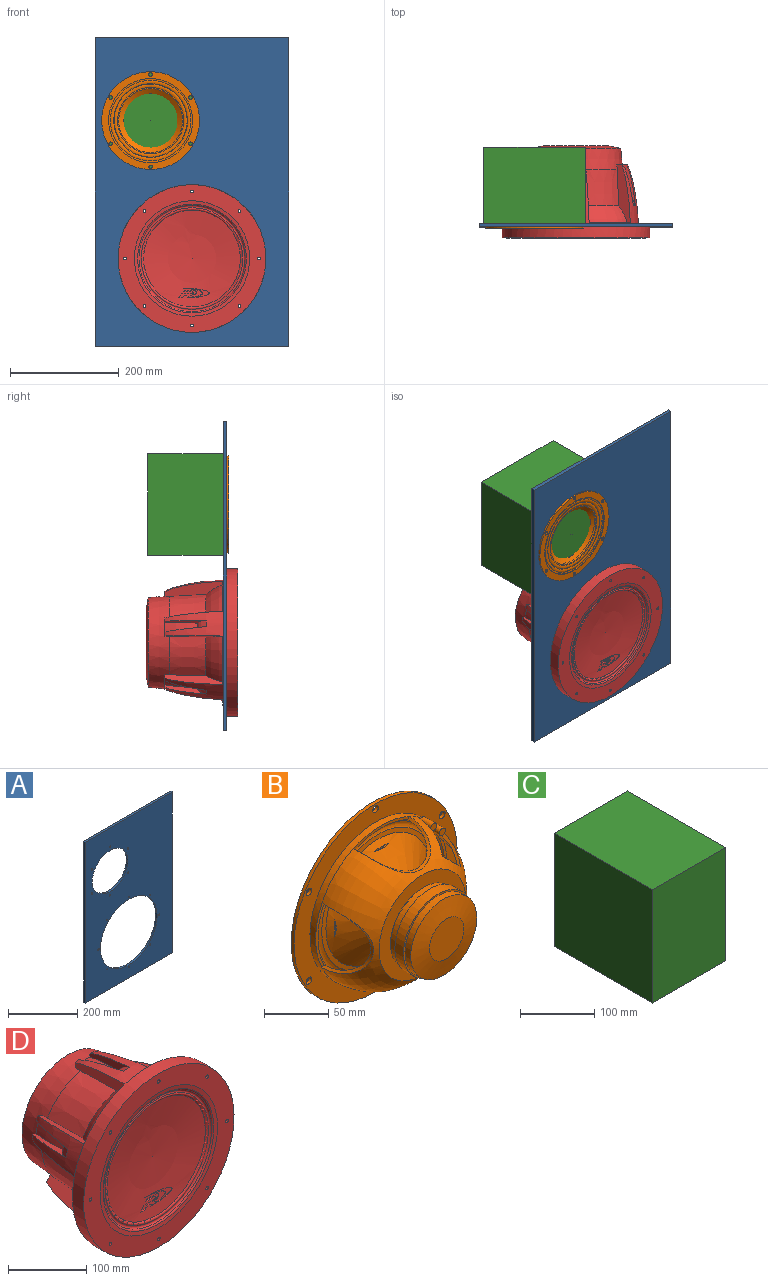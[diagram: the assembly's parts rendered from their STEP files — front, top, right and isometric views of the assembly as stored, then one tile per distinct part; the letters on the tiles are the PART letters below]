
ASSEMBLY  parts=4 mates=2
PART A: 22 faces, bbox 355.6x6.4x567.8 mm
  f0: plane 567.8x6.35mm, normal (-1,0,0), area 3605.5mm2, adj f1,f3,f4,f5
  f1: plane 355.6x6.35mm, normal (0,0,1), area 2258.1mm2, adj f0,f2,f4,f5
  f2: plane 567.8x6.35mm, normal (1,0,0), area 3605.5mm2, adj f1,f3,f4,f5
  f3: plane 355.6x6.35mm, normal (0,0,-1), area 2258.1mm2, adj f0,f2,f4,f5
  f4: plane 567.8x355.6mm, normal (0,1,0), area 143146.8mm2, adj f0,f1,f2,f3,f6,f7,f8,f9
  f5: plane 567.8x355.6mm, normal (0,-1,0), area 143146.8mm2, adj f0,f1,f2,f3,f6,f7,f8,f9
  f6: cylinder r=72.52mm len=145.03mm, axis (0,-1,0), area 2893.3mm2, adj f4,f5
  f7: cylinder r=2.38mm len=6.35mm, axis (0,-1,0), area 95mm2, adj f4,f5
  f8: cylinder r=2.38mm len=6.35mm, axis (0,-1,0), area 95mm2, adj f4,f5
  f9: cylinder r=2.38mm len=6.35mm, axis (0,-1,0), area 95mm2, adj f4,f5
  f10: cylinder r=2.38mm len=6.35mm, axis (0,-1,0), area 95mm2, adj f4,f5
  f11: cylinder r=2.38mm len=6.35mm, axis (0,-1,0), area 95mm2, adj f4,f5
  f12: cylinder r=2.38mm len=6.35mm, axis (0,-1,0), area 95mm2, adj f4,f5
  f13: cylinder r=2.38mm len=6.35mm, axis (0,-1,0), area 95mm2, adj f4,f5
  f14: cylinder r=3.17mm len=6.35mm, axis (0,-1,0), area 126.7mm2, adj f4,f5
  f15: cylinder r=3.17mm len=6.35mm, axis (0,-1,0), area 126.7mm2, adj f4,f5
  f16: cylinder r=3.17mm len=6.35mm, axis (0,-1,0), area 126.7mm2, adj f4,f5
  f17: cylinder r=115.5mm len=231mm, axis (0,-1,0), area 4608.2mm2, adj f4,f5
  f18: cylinder r=3.17mm len=6.35mm, axis (0,-1,0), area 126.7mm2, adj f4,f5
  f19: cylinder r=3.17mm len=6.35mm, axis (0,-1,0), area 126.7mm2, adj f4,f5
  f20: cylinder r=3.17mm len=6.35mm, axis (0,-1,0), area 126.7mm2, adj f4,f5
  f21: cylinder r=2.38mm len=6.35mm, axis (0,-1,0), area 95mm2, adj f4,f5
PART B: 78 faces, bbox 180.1x81.7x180.1 mm
  f0: plane 6.14x4.89mm, normal (0,-1,0), area 13mm2, adj f10,f38,f51,f69
  f1: plane 7.38x7.38mm, normal (0,-1,0), area 19.2mm2, adj f10,f38,f65,f69
  f2: plane 6.14x4.89mm, normal (0,-1,0), area 13mm2, adj f10,f38,f50,f65
  f3: plane 13.36x13.36mm, normal (0,-1,0), area 140.2mm2, adj f4
  f4: torus R=6.68mm, axis (0,-1,0), area 421.3mm2, adj f3,f5
  f5: cone r=13.01mm half-angle=54.8deg, axis (0,1,0), area 11955.4mm2, adj f4,f6,f19,f20,f54,f55,f58,f59
  f6: cone r=61.59mm half-angle=84.5deg, axis (0,1,0), area 1563.3mm2, adj f5,f7
  f7: torus R=64.94mm, axis (0,-1,0), area 2086.2mm2, adj f6,f8
  f8: torus R=67.45mm, axis (0,-1,0), area 994.8mm2, adj f7,f9
  f9: torus R=71.9mm, axis (0,-1,0), area 496.2mm2, adj f8,f10
  f10: cylinder r=69.98mm len=139.95mm, axis (0,-1,0), area 2383.7mm2, adj f0,f1,f2,f9,f11,f17,f52,f56
  f11: torus R=18.17mm, axis (0,-1,0), area 10126.2mm2, adj f10,f12,f18,f49,f50,f51,f53,f57
  f12: torus R=42.46mm, axis (0,-1,0), area 2789.7mm2, adj f11,f13
  f13: torus R=33.02mm, axis (0,-1,0), area 2169.8mm2, adj f12,f14
  f14: torus R=23.59mm, axis (0,-1,0), area 1549.9mm2, adj f13,f15
  f15: torus R=14.15mm, axis (0,-1,0), area 929.9mm2, adj f14,f16
  f16: torus R=4.72mm, axis (0,-1,0), area 310mm2, adj f15
  f17: plane 61.73x8.91mm, normal (0,-1,0), area 157.5mm2, adj f10,f18,f38
  f18: cone r=38.1mm half-angle=1deg, axis (0,1,0), area 339.7mm2, adj f11,f17,f37
  f19: cone r=38.1mm half-angle=1deg, axis (0,1,0), area 9.7mm2, adj f5,f20
  f20: plane 15.49x1.35mm, normal (0,-1,0), area 14mm2, adj f5,f19
  f21: torus R=9.58mm, axis (0,-1,0), area 22.9mm2, adj f22,f48
  f22: cone r=23.77mm half-angle=30deg, axis (0,1,0), area 2987.6mm2, adj f21,f23
  f23: plane 47.54x47.54mm, normal (0,1,0), area 43.5mm2, adj f22,f24
  f24: cone r=8.84mm half-angle=30deg, axis (0,1,0), area 2971.2mm2, adj f23,f25
  f25: torus R=8.67mm, axis (0,-1,0), area 25.6mm2, adj f24,f26
  f26: cone r=0mm half-angle=15deg, axis (0,-1,0), area 872.6mm2, adj f25
  f27: plane 38.1x38.1mm, normal (0,-1,0), area 1140.1mm2, adj f28
  f28: cone r=19.05mm half-angle=79.7deg, axis (0,1,0), area 3098.1mm2, adj f27,f29
  f29: cylinder r=36.51mm len=73.03mm, axis (0,-1,0), area 1456.8mm2, adj f28,f30
  f30: plane 76.2x76.2mm, normal (0,-1,0), area 372.1mm2, adj f29,f31
  f31: cylinder r=38.1mm len=76.2mm, axis (0,-1,0), area 2280.2mm2, adj f30,f32
  f32: plane 76.2x76.2mm, normal (0,1,0), area 372.1mm2, adj f31,f33
  f33: cylinder r=36.51mm len=73.03mm, axis (0,-1,0), area 1456.8mm2, adj f32,f34
  f34: plane 73.03x73.03mm, normal (0,1,0), area 286.3mm2, adj f33,f35
  f35: cylinder r=35.24mm len=70.49mm, axis (0,-1,0), area 281.2mm2, adj f34,f36
  f36: plane 95.89x95.89mm, normal (0,-1,0), area 3318.9mm2, adj f35,f37
  f37: torus R=18.17mm, axis (0,-1,0), area 10575mm2, adj f18,f36,f38,f49,f50,f51,f53,f57
  f38: cylinder r=72.52mm len=145.03mm, axis (0,-1,0), area 2893.3mm2, adj f0,f1,f2,f17,f37,f39,f52,f56
  f39: plane 180.09x180.09mm, normal (0,-1,0), area 8760.5mm2, adj f38,f40,f72,f73,f74,f75,f76,f77
  f40: cylinder r=90.04mm len=180.09mm, axis (0,-1,0), area 1796.3mm2, adj f39,f41
  f41: plane 180.09x180.09mm, normal (0,1,0), area 6488.4mm2, adj f40,f42,f72,f73,f74,f75,f76,f77
  f42: cylinder r=77.34mm len=154.69mm, axis (0,-1,0), area 617.2mm2, adj f41,f43
  f43: cone r=77.34mm half-angle=84.5deg, axis (0,1,0), area 1511.8mm2, adj f42,f44
  f44: torus R=71.9mm, axis (0,-1,0), area 2884.4mm2, adj f43,f45
  f45: torus R=67.45mm, axis (0,-1,0), area 279.6mm2, adj f44,f46
  f46: torus R=64.94mm, axis (0,-1,0), area 2601.4mm2, adj f45,f47
  f47: cone r=60.9mm half-angle=84.5deg, axis (0,1,0), area 778.2mm2, adj f46,f48
  f48: cone r=9.66mm half-angle=54.8deg, axis (0,1,0), area 12942.8mm2, adj f21,f47
  f49: plane 20.3x20.3mm, normal (0.71,0.02,0.71), area 99mm2, adj f11,f37,f50,f51
  f50: plane 38.95x12.32mm, normal (-0.71,0.02,0.71), area 107.3mm2, adj f2,f11,f37,f49
  f51: plane 38.95x12.32mm, normal (0.71,0.02,-0.71), area 107.3mm2, adj f0,f11,f37,f49
  f52: plane 61.73x8.91mm, normal (0,-1,0), area 157.5mm2, adj f10,f38,f53
  f53: cone r=38.1mm half-angle=1deg, axis (0,1,0), area 339.3mm2, adj f11,f37,f52
  f54: plane 15.49x1.35mm, normal (0,-1,0), area 14mm2, adj f5,f55
  f55: cone r=38.1mm half-angle=1deg, axis (0,1,0), area 9.7mm2, adj f5,f54
  f56: plane 61.73x8.91mm, normal (0,-1,0), area 157.5mm2, adj f10,f38,f57
  f57: cone r=38.1mm half-angle=1deg, axis (0,1,0), area 339.3mm2, adj f11,f37,f56
  f58: plane 15.49x1.35mm, normal (0,-1,0), area 14mm2, adj f5,f59
  f59: cone r=38.1mm half-angle=1deg, axis (0,1,0), area 9.7mm2, adj f5,f58
  f60: plane 61.73x8.91mm, normal (0,-1,0), area 157.5mm2, adj f10,f38,f61
  f61: cone r=38.1mm half-angle=1deg, axis (0,1,0), area 339.3mm2, adj f11,f37,f60
  f62: plane 15.49x1.35mm, normal (0,-1,0), area 14mm2, adj f5,f63
  f63: cone r=38.1mm half-angle=1deg, axis (0,1,0), area 9.7mm2, adj f5,f62
  f64: plane 4.41x3.83mm, normal (0,1,0), area 6.6mm2, adj f38,f65
  f65: cone r=3.17mm half-angle=1deg, axis (0,-1,0), area 262.2mm2, adj f1,f2,f64,f66,f67
  f66: plane 6.79x6.79mm, normal (0,-1,0), area 36.2mm2, adj f65
  f67: plane 4.8x4.24mm, normal (0,1,0), area 9.4mm2, adj f10,f65
  f68: plane 4.41x3.83mm, normal (0,1,0), area 6.6mm2, adj f38,f69
  f69: cone r=3.17mm half-angle=1deg, axis (0,-1,0), area 262.2mm2, adj f0,f1,f68,f70,f71
  f70: plane 6.79x6.79mm, normal (0,-1,0), area 36.2mm2, adj f69
  f71: plane 4.8x4.24mm, normal (0,1,0), area 9.4mm2, adj f10,f69
  f72: cylinder r=3.17mm len=6.35mm, axis (0,1,0), area 63.3mm2, adj f39,f41
  f73: cylinder r=3.17mm len=6.35mm, axis (0,1,0), area 63.3mm2, adj f39,f41
  f74: cylinder r=3.17mm len=6.35mm, axis (0,1,0), area 63.3mm2, adj f39,f41
  f75: cylinder r=3.17mm len=6.35mm, axis (0,1,0), area 63.3mm2, adj f39,f41
  f76: cylinder r=3.17mm len=6.35mm, axis (0,1,0), area 63.3mm2, adj f39,f41
  f77: cylinder r=3.17mm len=6.35mm, axis (0,1,0), area 63.3mm2, adj f39,f41
PART C: 6 faces, bbox 139.7x187.3x187.3 mm
  f0: plane 187.33x187.33mm, normal (1,0,0), area 35090.7mm2, adj f1,f2,f3,f4
  f1: plane 187.33x139.7mm, normal (0,0,-1), area 26169.3mm2, adj f0,f2,f3,f5
  f2: plane 187.33x139.7mm, normal (0,-1,0), area 26169.3mm2, adj f0,f1,f4,f5
  f3: plane 187.33x139.7mm, normal (0,1,0), area 26169.3mm2, adj f0,f1,f4,f5
  f4: plane 187.33x139.7mm, normal (0,0,1), area 26169.3mm2, adj f0,f2,f3,f5
  f5: plane 187.33x187.33mm, normal (-1,0,0), area 35090.7mm2, adj f1,f2,f3,f4
PART D: 90 faces, bbox 274.1x171.5x274.1 mm
  f0: cylinder r=2.38mm len=20.4mm, axis (0,-1,0), area 305.2mm2, adj f8,f68
  f1: cylinder r=2.38mm len=20.4mm, axis (0,-1,0), area 305.2mm2, adj f8,f68
  f2: cylinder r=2.38mm len=20.4mm, axis (0,-1,0), area 305.2mm2, adj f8,f68
  f3: cylinder r=2.38mm len=20.4mm, axis (0,-1,0), area 305.2mm2, adj f8,f68
  f4: cylinder r=2.38mm len=20.4mm, axis (0,-1,0), area 305.2mm2, adj f8,f68
  f5: cylinder r=2.38mm len=20.4mm, axis (0,-1,0), area 305.2mm2, adj f8,f68
  f6: cylinder r=2.38mm len=20.4mm, axis (0,-1,0), area 305.2mm2, adj f8,f68
  f7: cylinder r=136mm len=272mm, axis (0,-1,0), area 17432.1mm2, adj f8,f68
  f8: plane 272x272mm, normal (0,1,0), area 16054.8mm2, adj f0,f1,f2,f3,f4,f5,f6,f7
  f9: plane 108.77x32.45mm, normal (0.1,0.03,-1), area 1820.9mm2, adj f11,f12,f54,f65,f66,f67
  f10: plane 108.77x26.73mm, normal (-0.51,0.03,0.86), area 1820.9mm2, adj f11,f12,f18,f57,f58,f67
  f11: revolved ~229.77x229.77mm, area 27825.5mm2, adj f8,f9,f10,f12,f13,f16,f17,f18
  f12: plane 33.43x19.28mm, normal (0,1,0), area 215.5mm2, adj f9,f10,f11,f15,f16,f17,f67
  f13: revolved ~15.59x15mm, area 225.3mm2, adj f11,f14,f16,f17
  f14: plane 13.54x9.57mm, normal (0,1,0), area 74.8mm2, adj f13,f15,f16,f17
  f15: revolved ~60.59x21.55mm, area 976.2mm2, adj f12,f14,f16,f17
  f16: plane 77.08x22.87mm, normal (-0.25,0.07,0.97), area 645.7mm2, adj f11,f12,f13,f14,f15
  f17: plane 77.1x25.27mm, normal (0.37,0.07,-0.93), area 645.7mm2, adj f11,f12,f13,f14,f15
  f18: plane 77.24x58.57mm, normal (0,1,0), area 653.6mm2, adj f10,f11,f19,f57
  f19: plane 108.77x31mm, normal (0.98,0.03,-0.22), area 1820.9mm2, adj f11,f18,f21,f57,f58,f67
  f20: plane 108.77x31.01mm, normal (-0.98,0.03,-0.22), area 1820.9mm2, adj f11,f21,f27,f59,f60,f67
  f21: plane 34.13x10.9mm, normal (0,1,0), area 215.5mm2, adj f11,f19,f20,f24,f25,f26,f67
  f22: revolved ~15x13.82mm, area 225.3mm2, adj f11,f23,f25,f26
  f23: plane 12.63x6.28mm, normal (0,1,0), area 74.8mm2, adj f22,f24,f25,f26
  f24: revolved ~60.59x21.04mm, area 976.2mm2, adj f21,f23,f25,f26
  f25: plane 77.08x25.22mm, normal (-1,0.07,0.06), area 645.7mm2, adj f11,f21,f22,f23,f24
  f26: plane 77.1x25.24mm, normal (1,0.07,0.06), area 645.7mm2, adj f11,f21,f22,f23,f24
  f27: plane 77.24x58.57mm, normal (0,1,0), area 653.6mm2, adj f11,f20,f28,f59
  f28: plane 108.77x26.73mm, normal (0.51,0.03,0.86), area 1820.9mm2, adj f11,f27,f30,f59,f60,f67
  f29: plane 108.77x32.46mm, normal (-0.1,0.03,-1), area 1820.9mm2, adj f11,f30,f36,f61,f62,f67
  f30: plane 33.43x19.28mm, normal (0,1,0), area 215.5mm2, adj f11,f28,f29,f33,f34,f35,f67
  f31: revolved ~15.59x15mm, area 225.3mm2, adj f11,f32,f34,f35
  f32: plane 13.54x9.57mm, normal (0,1,0), area 74.8mm2, adj f31,f33,f34,f35
  f33: revolved ~60.59x21.55mm, area 976.2mm2, adj f30,f32,f34,f35
  f34: plane 77.08x25.24mm, normal (-0.37,0.07,-0.93), area 645.7mm2, adj f11,f30,f31,f32,f33
  f35: plane 77.1x22.89mm, normal (0.25,0.07,0.97), area 645.7mm2, adj f11,f30,f31,f32,f33
  f36: plane 89.02x34.78mm, normal (0,1,0), area 653.6mm2, adj f11,f29,f37,f61
  f37: plane 108.77x26.59mm, normal (-0.66,0.03,0.75), area 1820.9mm2, adj f11,f36,f39,f61,f62,f67
  f38: plane 108.77x30.93mm, normal (0.92,0.03,-0.4), area 1820.9mm2, adj f11,f39,f45,f63,f64,f67
  f39: plane 31.65x26.78mm, normal (0,1,0), area 215.5mm2, adj f11,f37,f38,f42,f43,f44,f67
  f40: revolved ~16.42x15.64mm, area 225.3mm2, adj f11,f41,f43,f44
  f41: plane 13.5x12.13mm, normal (0,1,0), area 74.8mm2, adj f40,f42,f43,f44
  f42: revolved ~60.59x20.76mm, area 976.2mm2, adj f39,f41,f43,f44
  f43: plane 77.08x22.95mm, normal (0.77,0.07,-0.63), area 645.7mm2, adj f11,f39,f40,f41,f42
  f44: plane 77.1x18.57mm, normal (-0.84,0.07,0.54), area 645.7mm2, adj f11,f39,f40,f41,f42
  f45: plane 93.6x16.33mm, normal (0,1,0), area 653.6mm2, adj f11,f38,f46,f63
  f46: plane 108.77x30.93mm, normal (-0.92,0.03,-0.4), area 1820.9mm2, adj f11,f45,f48,f63,f64,f67
  f47: plane 108.77x26.59mm, normal (0.66,0.03,0.75), area 1820.9mm2, adj f11,f48,f54,f65,f66,f67
  f48: plane 31.65x26.78mm, normal (0,1,0), area 215.5mm2, adj f11,f46,f47,f51,f52,f53,f67
  f49: revolved ~16.42x15.64mm, area 225.3mm2, adj f11,f50,f52,f53
  f50: plane 13.5x12.13mm, normal (0,1,0), area 74.8mm2, adj f49,f51,f52,f53
  f51: revolved ~60.59x20.76mm, area 976.2mm2, adj f48,f50,f52,f53
  f52: plane 77.08x18.55mm, normal (0.84,0.07,0.54), area 645.7mm2, adj f11,f48,f49,f50,f51
  f53: plane 77.1x22.97mm, normal (-0.77,0.07,-0.63), area 645.7mm2, adj f11,f48,f49,f50,f51
  f54: plane 89.02x34.78mm, normal (0,1,0), area 653.6mm2, adj f9,f11,f47,f65
  f55: plane 120.64x120.64mm, normal (0,1,0), area 11430.8mm2, adj f56
  f56: cone r=60.32mm half-angle=78.8deg, axis (0,-1,0), area 10145.7mm2, adj f55,f67
  f57: revolved ~76.51x61.88mm, area 3089.9mm2, adj f10,f18,f19,f58
  f58: cone r=86.07mm half-angle=3.6deg, axis (0,-1,0), area 5167.8mm2, adj f10,f19,f57,f67
  f59: revolved ~76.51x61.88mm, area 3089.9mm2, adj f20,f27,f28,f60
  f60: cone r=86.07mm half-angle=3.6deg, axis (0,-1,0), area 5167.8mm2, adj f20,f28,f59,f67
  f61: revolved ~85.72x41.9mm, area 3089.9mm2, adj f29,f36,f37,f62
  f62: cone r=86.07mm half-angle=3.6deg, axis (0,-1,0), area 5167.8mm2, adj f29,f37,f61,f67
  f63: revolved ~90.13x31.16mm, area 3089.9mm2, adj f38,f45,f46,f64
  f64: cone r=86.07mm half-angle=3.6deg, axis (0,-1,0), area 5167.8mm2, adj f38,f46,f63,f67
  f65: revolved ~85.72x41.9mm, area 3089.9mm2, adj f9,f47,f54,f66
  f66: cone r=86.07mm half-angle=3.6deg, axis (0,-1,0), area 5167.8mm2, adj f9,f47,f65,f67
  f67: cone r=82.5mm half-angle=5.2deg, axis (0,-1,0), area 19611.9mm2, adj f9,f10,f12,f19,f20,f21,f28,f29
  f68: plane 272x272mm, normal (0,-1,0), area 22539.8mm2, adj f0,f1,f2,f3,f4,f5,f6,f7
  f69: cylinder r=2.38mm len=20.4mm, axis (0,-1,0), area 305.2mm2, adj f8,f68
  f70: cone r=106.19mm half-angle=83.4deg, axis (0,-1,0), area 3927.7mm2, adj f68,f71
  f71: torus R=100.51mm, axis (0,-1,0), area 1925.6mm2, adj f70,f72
  f72: torus R=95.04mm, axis (0,-1,0), area 3125.9mm2, adj f71,f73
  f73: torus R=91.74mm, axis (0,-1,0), area 2970mm2, adj f72,f74
  f74: sphere r=600mm, area 24610.5mm2, adj f73,f75,f76,f77,f78,f79,f80,f81
  f75: plane 9.28x4.68mm, normal (0.43,0,0.9), area 9.9mm2, adj f74,f76,f88,f89
  f76: extruded ~4.53x1.09mm, area 4.6mm2, adj f74,f75,f77,f89
  f77: extruded ~47.88x16.81mm, area 91.7mm2, adj f74,f76,f78,f89
  f78: extruded ~35.88x15.54mm, area 56.6mm2, adj f74,f77,f79,f89
  f79: plane 6.47x3.57mm, normal (-0.48,0,-0.88), area 7.4mm2, adj f74,f78,f80,f89
  f80: extruded ~11.35x8.28mm, area 21.3mm2, adj f74,f79,f81,f89
  f81: plane 15.82x1.16mm, normal (0,0,-1), area 15.9mm2, adj f74,f80,f82,f89
  f82: plane 2.28x2.1mm, normal (0.74,0,-0.68), area 3.1mm2, adj f74,f81,f83,f89
  f83: plane 16.85x2.25mm, normal (0,0,1), area 15.9mm2, adj f74,f82,f84,f89
  f84: extruded ~6.12x3.81mm, area 10.2mm2, adj f74,f83,f85,f89
  f85: plane 16.79x2.28mm, normal (0,0,-1), area 15.9mm2, adj f74,f84,f86,f89
  f86: plane 7.05x6.51mm, normal (0.74,0,-0.68), area 9.3mm2, adj f74,f85,f87,f89
  f87: plane 9.13x1.6mm, normal (0,0,1), area 8.9mm2, adj f74,f86,f88,f89
  f88: plane 4.73x4.55mm, normal (-0.72,0,0.69), area 6.4mm2, adj f74,f75,f87,f89
  f89: sphere r=601mm, area 401mm2, adj f75,f76,f77,f78,f79,f80,f81,f82
PLACE A at identity
PLACE B rot(axis=(1,0,0),180deg) t=(-76.2,103.89,254)mm
PLACE C rot(axis=(0.58,-0.58,-0.58),120deg) t=(-76.2,108.65,254)mm
PLACE D at identity fixed
MATE fastened D.f7 <-> B.f39  axis (0,1,0) through (0,25.4,0)mm
MATE fastened C.f0 <-> A.f6  axis (0,-1,0) through (-76.2,31.75,254)mm
